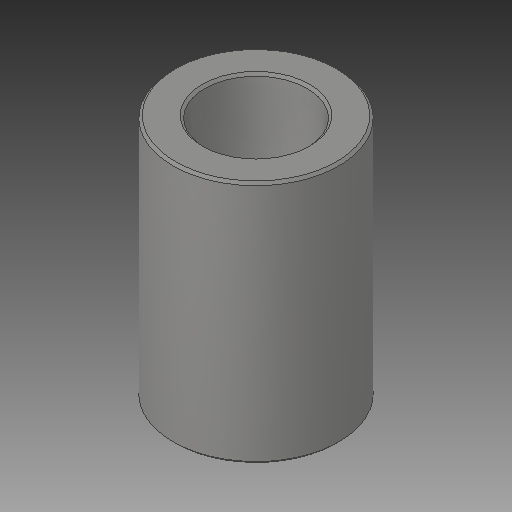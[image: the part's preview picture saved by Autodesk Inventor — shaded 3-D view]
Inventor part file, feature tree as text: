
AUTODESK INVENTOR PART (.ipt)
format: ipt  version: 2019 (Build 230136000, 136)  size: 104,960 bytes
history: native  units: in
note: dims shown in document units (in); Inventor stores cm internally (conversion verified against a paired STEP export)
features: chamfer x1
ambient origin geometry x8: Origin, YZ Plane, XZ Plane, XY Plane, X Axis, Y Axis, Z Axis, Center Point
bodies: Solid1 (feature_tree)
feature tree (1):
  chamfer  "Chamfer1"  [1 undecoded]
note: 1 required parameter value undecoded (feature->parameter linkage not recoverable at this tier; creation-order binding heuristic only, values carry confidence <= 0.55)
